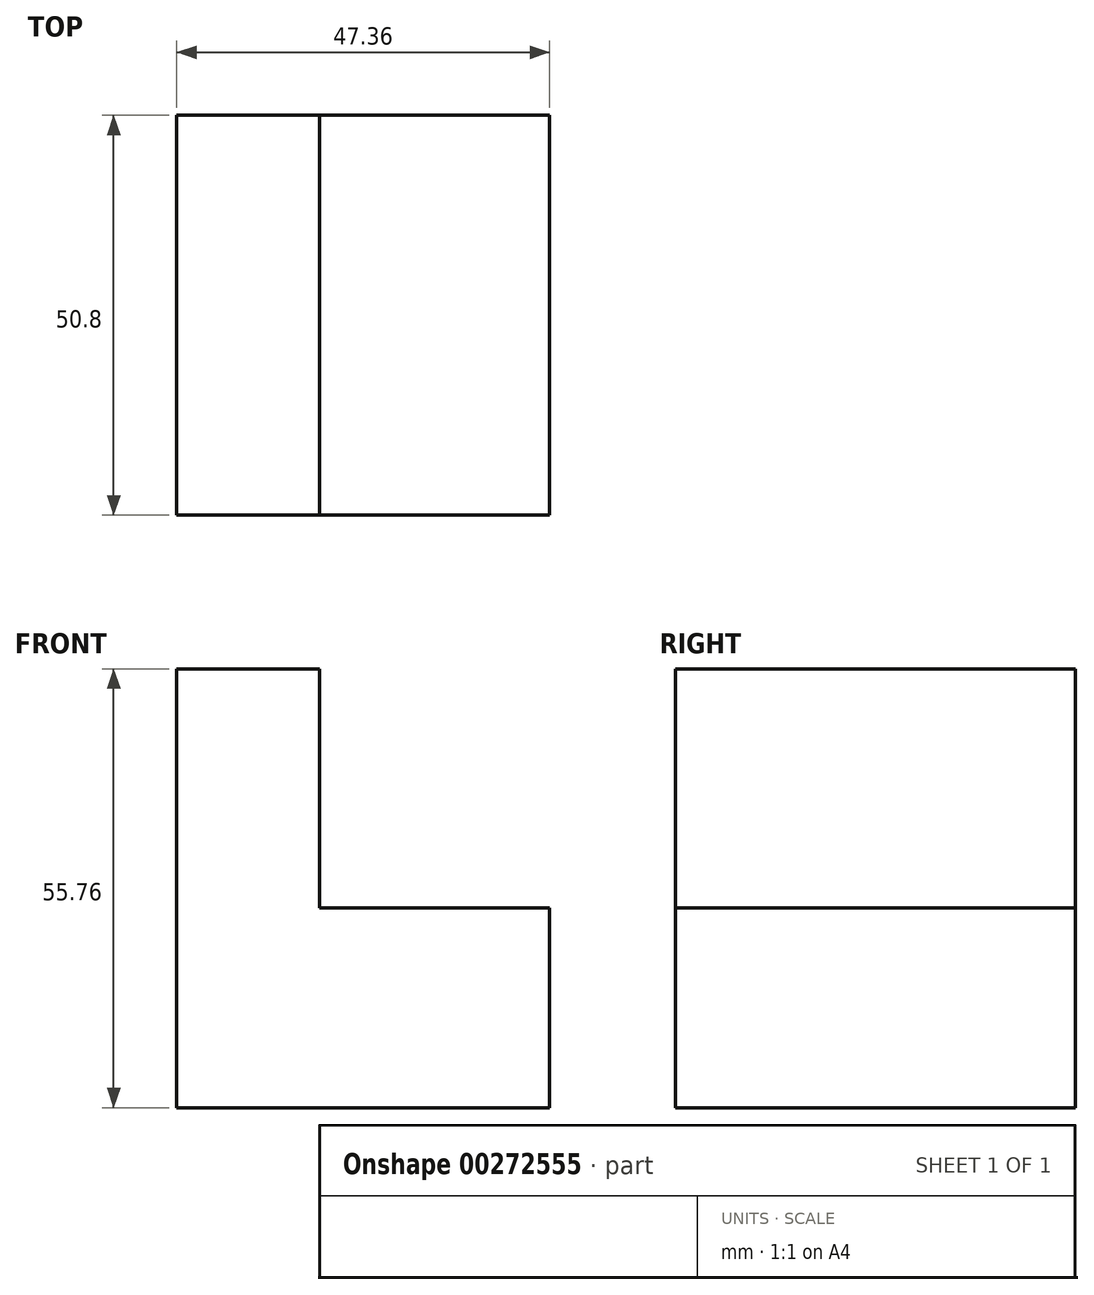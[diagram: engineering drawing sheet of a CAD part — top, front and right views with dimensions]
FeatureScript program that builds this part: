
annotation { "Feature Type Name" : "Feature", "Feature Type Description" : "" }
export const myFeature = defineFeature(function(context is Context, id is Id, definition is map)
    precondition{}
    {
        {
            var Q0;
            Q0=qCreatedBy(makeId("Front.planeOp"),FACE);
            var sketch = newSketch(context, id + "F0", { "sketchPlane" : qUnion([Q0])});
            skLineSegment(sketch, "E0", {"start": v(0, 0) * mm, "end": v(-47.36, 0) * mm});
            skLineSegment(sketch, "E1", {"start": v(-47.36, 0) * mm, "end": v(-47.36, 55.76) * mm});
            skLineSegment(sketch, "E2", {"start": v(-47.36, 55.76) * mm, "end": v(-29.22, 55.76) * mm});
            skLineSegment(sketch, "E3", {"start": v(-29.22, 55.76) * mm, "end": v(-29.22, 25.4) * mm});
            skLineSegment(sketch, "E4", {"start": v(-29.22, 25.4) * mm, "end": v(0, 25.4) * mm});
            skLineSegment(sketch, "E5", {"start": v(0, 25.4) * mm, "end": v(0, 0) * mm});
            skSolve(sketch);
        }
        {
            var Q0;
            Q0=makeQuery(id+"F0.imprint","IMPRINT",FACE,{"disambiguationData":[TD([[makeQuery(id+"F0.imprint","IMPRINT",EDGE,{"derivedFrom":sQuery(id+"F0.wireOp",EDGE,"E0")}),-1.0]])]});
            var sketch = newSketch(context, id + "F1", { "sketchPlane" : qUnion([Q0])});
            skSolve(sketch);
        }
        {
            var Q0;
            Q0 = qSketchRegion(id + "F1", true);
            var Q1;
            Q1=makeQuery(id+"F0.imprint","IMPRINT",FACE,{"disambiguationData":[TD([[makeQuery(id+"F0.imprint","IMPRINT",EDGE,{"derivedFrom":sQuery(id+"F0.wireOp",EDGE,"E0")}),-1.0]])]});
            extrude(context, id + "F2", {"entities" : qUnion([Q0, Q1]), "depth" : 50.8 * mm});
        }
    });
